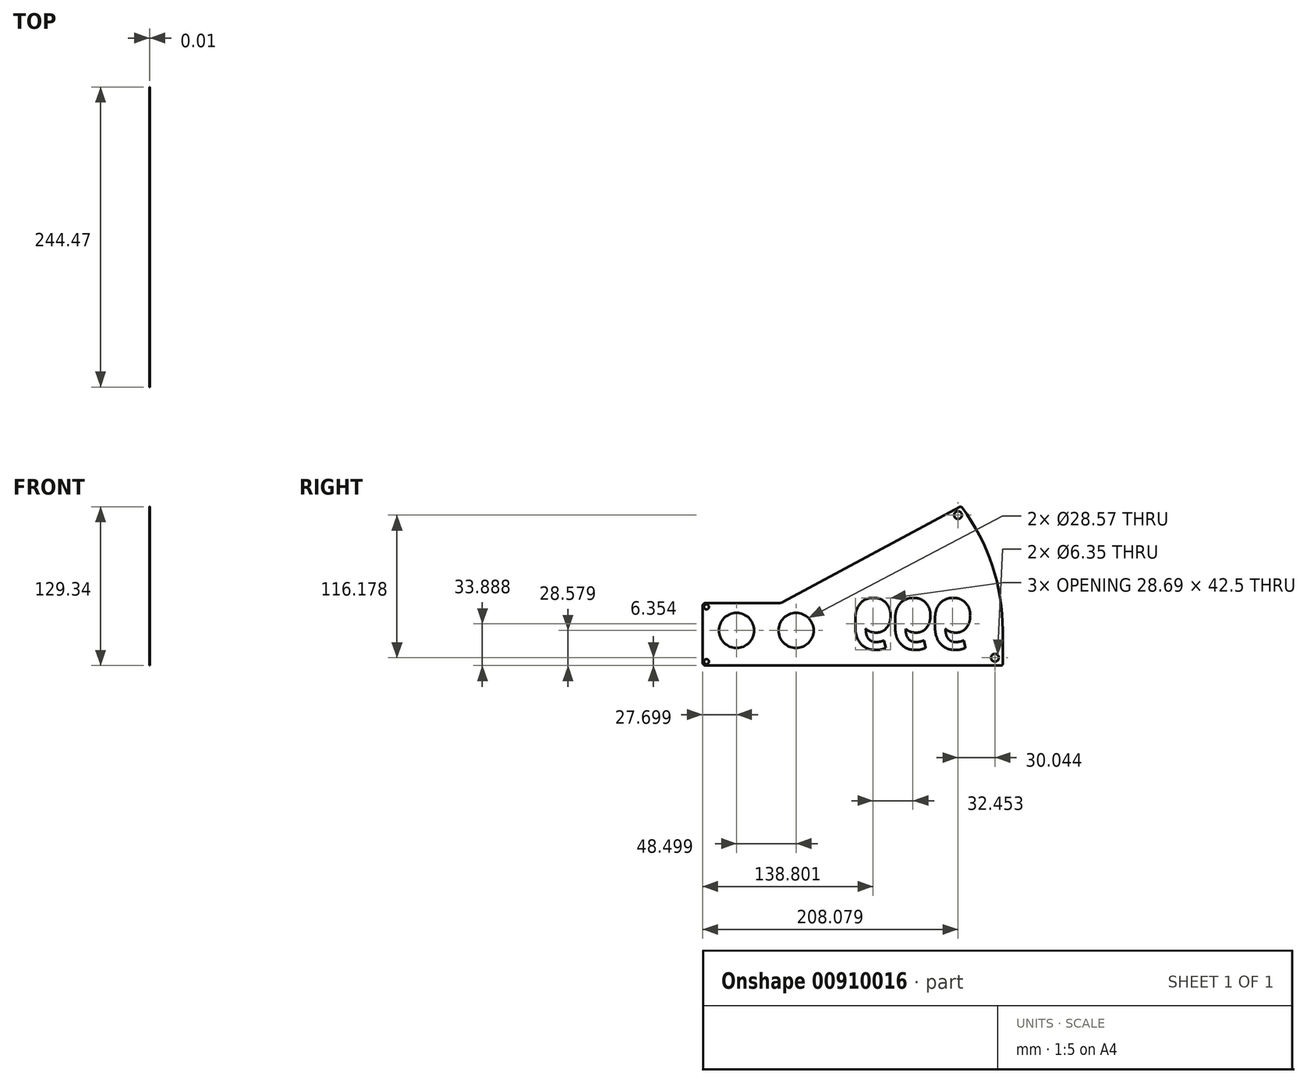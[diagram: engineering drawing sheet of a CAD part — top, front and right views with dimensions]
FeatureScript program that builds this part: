
annotation { "Feature Type Name" : "Feature", "Feature Type Description" : "" }
export const myFeature = defineFeature(function(context is Context, id is Id, definition is map)
    precondition{}
    {
        {
            var Q0;
            Q0=qCreatedBy(makeId("Right.planeOp"),FACE);
            var sketch = newSketch(context, id + "F0", { "sketchPlane" : qUnion([Q0])});
            skCircle(sketch, "E0", {"center": v(-61.81, 24.36) * mm, "radius": 14.29 * mm});
            skCircle(sketch, "E1", {"center": v(-61.81, 24.36) * mm, "radius": 25.4 * mm});
            skLineSegment(sketch, "E2", {"start": v(-61.81, -4.22) * mm, "end": v(105.2, -4.22) * mm});
            skArc(sketch, "E3", {"start": v(106.46, 24.36) * mm, "mid": v(97.97, 77.15) * mm, "end": v(73.34, 124.6) * mm});
            skLineSegment(sketch, "E4", {"start": v(106.46, -2.95) * mm, "end": v(106.46, 24.36) * mm});
            skLineSegment(sketch, "E5", {"start": v(71.72, 124.97) * mm, "end": v(-72.43, 47.49) * mm});
            skPoint(sketch, "E6.visualSharp", {"position": v(106.46, -4.22) * mm});
            skArc(sketch, "E6.filletArc", {"start": v(105.2, -4.22) * mm, "mid": v(106.1, -3.84) * mm, "end": v(106.46, -2.95) * mm});
            skPoint(sketch, "E7.visualSharp", {"position": v(72.69, 125.49) * mm});
            skArc(sketch, "E7.filletArc", {"start": v(73.34, 124.6) * mm, "mid": v(72.6, 125.09) * mm, "end": v(71.72, 124.97) * mm});
            skCircle(sketch, "E8", {"center": v(70.07, 118.31) * mm, "radius": 3.17 * mm});
            skCircle(sketch, "E9", {"center": v(100.11, 2.13) * mm, "radius": 3.17 * mm});
            skArc(sketch, "E10", {"start": v(93.76, 24.36) * mm, "mid": v(85.44, 74.57) * mm, "end": v(61.36, 119.4) * mm});
            skLineSegment(sketch, "E11", {"start": v(-87.21, -4.22) * mm, "end": v(-61.81, -4.22) * mm});
            skLineSegment(sketch, "E12", {"start": v(93.76, 24.36) * mm, "end": v(93.76, -4.22) * mm});
            skLineSegment(sketch, "E13", {"start": v(-87.21, -4.22) * mm, "end": v(-135.47, -4.22) * mm});
            skLineSegment(sketch, "E14", {"start": v(-138.01, -1.68) * mm, "end": v(-138.01, 44.2) * mm});
            skLineSegment(sketch, "E15", {"start": v(-135.47, 46.73) * mm, "end": v(-75.44, 46.73) * mm});
            skPoint(sketch, "E16.visualSharp", {"position": v(-138.01, 46.73) * mm});
            skArc(sketch, "E16.filletArc", {"start": v(-135.47, 46.73) * mm, "mid": v(-137.27, 45.99) * mm, "end": v(-138.01, 44.2) * mm});
            skPoint(sketch, "E17.visualSharp", {"position": v(-73.84, 46.73) * mm});
            skArc(sketch, "E17.filletArc", {"start": v(-75.44, 46.73) * mm, "mid": v(-73.89, 46.92) * mm, "end": v(-72.43, 47.49) * mm});
            skPoint(sketch, "E18.visualSharp", {"position": v(-138.01, -4.22) * mm});
            skArc(sketch, "E18.filletArc", {"start": v(-138.01, -1.68) * mm, "mid": v(-137.27, -3.47) * mm, "end": v(-135.47, -4.22) * mm});
            skPoint(sketch, "E19.start.orphan", {"position": v(-87.21, 24.36) * mm});
            skCircle(sketch, "E20", {"center": v(-110.31, 24.36) * mm, "radius": 14.29 * mm});
            skCircle(sketch, "E21", {"center": v(-134.84, -1.04) * mm, "radius": 2.03 * mm});
            skCircle(sketch, "E22", {"center": v(-134.84, 43.56) * mm, "radius": 2.03 * mm});
            skSolve(sketch);
        }
        {
            var Q0;
            Q0=qSketchRegion(id+"F0",true);
            var Q1;
            Q1=makeQuery(id+"F0.imprint","IMPRINT",FACE,{"disambiguationData":[TD([[makeQuery(id+"F0.imprint","IMPRINT",EDGE,{"derivedFrom":sQuery(id+"F0.wireOp",EDGE,"E0")}),-1.0]])]});
            extrude(context, id + "F1", {"entities" : qUnion([Q0, Q1]), "depth" : 3 / 203.2 * mm, "offsetDistance" : 25.4 * mm});
        }
        {
            var Q0;
            Q0=makeQuery(id+"F1.opExtrude","CAP_FACE",FACE,{"disambiguationData":[OSD([sQuery(id+"F0.wireOp",EDGE,"E0"),sQuery(id+"F0.wireOp",EDGE,"E2"),sQuery(id+"F0.wireOp",EDGE,"E3"),sQuery(id+"F0.wireOp",EDGE,"E4"),sQuery(id+"F0.wireOp",EDGE,"E5"),sQuery(id+"F0.wireOp",EDGE,"E6.filletArc"),sQuery(id+"F0.wireOp",EDGE,"E7.filletArc"),sQuery(id+"F0.wireOp",EDGE,"E8"),sQuery(id+"F0.wireOp",EDGE,"E9"),sQuery(id+"F0.wireOp",EDGE,"E11"),sQuery(id+"F0.wireOp",EDGE,"E13"),sQuery(id+"F0.wireOp",EDGE,"E14"),sQuery(id+"F0.wireOp",EDGE,"E15"),sQuery(id+"F0.wireOp",EDGE,"E16.filletArc"),sQuery(id+"F0.wireOp",EDGE,"E17.filletArc"),sQuery(id+"F0.wireOp",EDGE,"E18.filletArc"),sQuery(id+"F0.wireOp",EDGE,"E20"),sQuery(id+"F0.wireOp",EDGE,"E21"),sQuery(id+"F0.wireOp",EDGE,"E22")])],"isStart":true});
            var sketch = newSketch(context, id + "F2", { "sketchPlane" : qUnion([Q0])});
            skText(sketch, "E23", { "text": "666\n", "fontName": "RobotoSlab-Bold.ttf"});
            const initialGuessF2  = {"E23": [0.01613, 0.05032, -1, 0, 0.04183]};
            skSetInitialGuess(sketch, initialGuessF2);
            skSolve(sketch);
        }
        {
            var Q0;
            Q0 = qSketchRegion(id + "F2", true);
            var Q1;
            Q1=makeQuery(id+"F2.imprint","IMPRINT",FACE,{"disambiguationData":[TD([[makeQuery(id+"F2.imprint","IMPRINT",EDGE,{"derivedFrom":sQuery(id+"F2.wireOp",EDGE,"E23.sketch_text.stroke-75")}),1.0]])]});
            var Q2;
            Q2=makeQuery(id+"F2.imprint","IMPRINT",FACE,{"disambiguationData":[TD([[makeQuery(id+"F2.imprint","IMPRINT",EDGE,{"derivedFrom":sQuery(id+"F2.wireOp",EDGE,"E23.sketch_text.stroke-47")}),1.0]])]});
            var Q3;
            Q3=makeQuery(id+"F2.imprint","IMPRINT",FACE,{"disambiguationData":[TD([[makeQuery(id+"F2.imprint","IMPRINT",EDGE,{"derivedFrom":sQuery(id+"F2.wireOp",EDGE,"E23.sketch_text.stroke-19")}),1.0]])]});
            extrude(context, id + "F3", {"entities" : qUnion([Q0, Q1, Q2, Q3]), "operationType" : NewBodyOperationType.REMOVE, "oppositeDirection" : true, "depth" : 25.4 * mm, "offsetDistance" : 25.4 * mm});
        }
    });
